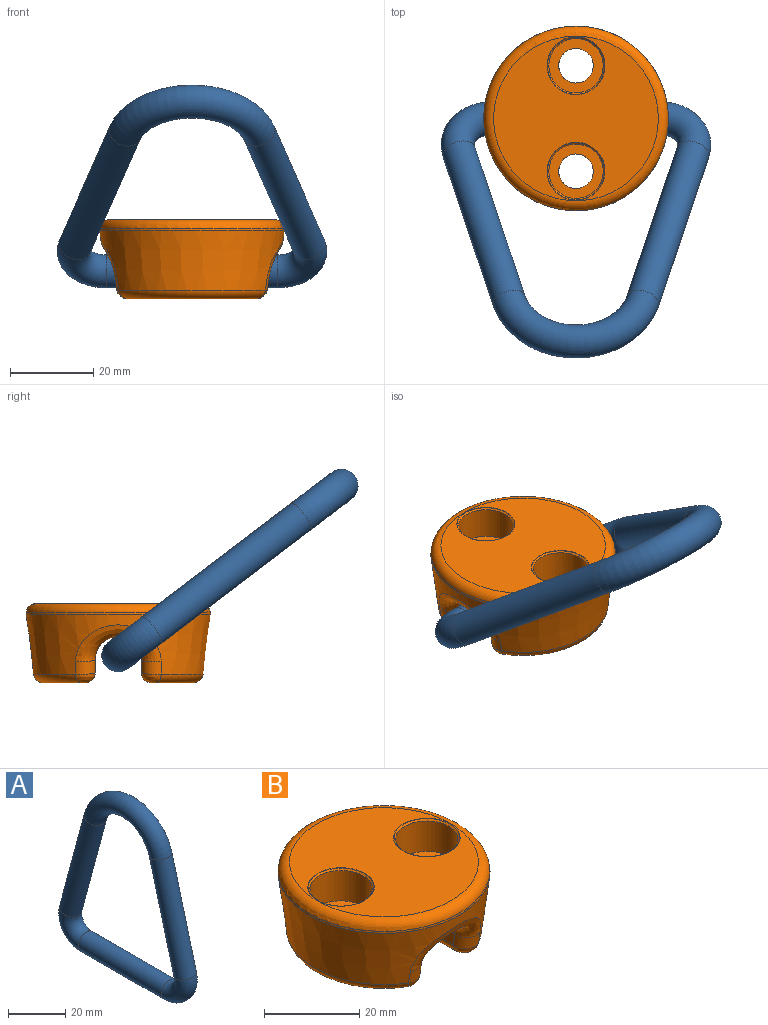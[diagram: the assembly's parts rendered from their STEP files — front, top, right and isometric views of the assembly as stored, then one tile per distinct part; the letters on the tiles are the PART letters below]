
ASSEMBLY  parts=2 mates=1
PART A: 6 faces, bbox 7.9x66.8x78.1 mm
  f0: cylinder r=3.97mm len=47.18mm, axis (0,0.26,0.97), area 1164.9mm2, adj f1,f5
  f1: torus R=7.94mm, axis (-1,0,0), area 362.7mm2, adj f0,f2
  f2: cylinder r=3.97mm len=41.05mm, axis (0,-1,0), area 1023.6mm2, adj f1,f3
  f3: torus R=7.94mm, axis (-1,0,0), area 362.7mm2, adj f2,f4
  f4: cylinder r=3.97mm len=47.18mm, axis (0,0.26,-0.97), area 1164.9mm2, adj f3,f5
  f5: torus R=16.67mm, axis (1,0,0), area 1088.2mm2, adj f0,f4
PART B: 44 faces, bbox 48x48x32 mm
  f0: plane 39.61x39.61mm, normal (0,0,1), area 926.8mm2, adj f22,f42,f43
  f1: cylinder r=5.56mm len=30.74mm, axis (0,1,0), area 274.6mm2, adj f6,f7,f9,f12,f32,f33,f34,f35
  f2: plane 31.44x10.14mm, normal (0,0,-1), area 170mm2, adj f14,f15,f16,f17,f39
  f3: cone r=22.23mm half-angle=7deg, axis (0,0,-1), area 63.1mm2, adj f4,f22
  f4: cone r=22.23mm half-angle=7deg, axis (0,0,1), area 1520.3mm2, adj f3,f8,f9,f10,f11,f12,f13,f16
  f5: plane 31.44x10.14mm, normal (0,0,-1), area 170mm2, adj f18,f19,f20,f21,f38
  f6: plane 30.74x3.18mm, normal (1,0,0), area 96.2mm2, adj f1,f8,f13,f15
  f7: plane 30.74x3.18mm, normal (-1,0,0), area 96.2mm2, adj f1,f10,f11,f20
  f8: bspline ~26.1x8.53mm, area 21mm2, adj f4,f6,f9,f17
  f9: bspline ~20.6x10.49mm, area 128mm2, adj f1,f4,f8,f10
  f10: bspline ~32.03x9.37mm, area 20.9mm2, adj f4,f7,f9,f21
  f11: bspline ~26.1x8.53mm, area 21mm2, adj f4,f7,f12,f18
  f12: bspline ~20.6x10.49mm, area 128mm2, adj f1,f4,f11,f13
  f13: bspline ~32.03x9.37mm, area 20.9mm2, adj f4,f6,f12,f14
  f14: bspline ~5.36x3.34mm, area 16.6mm2, adj f2,f13,f15,f16
  f15: cylinder r=2.39mm len=29.84mm, axis (0,-1,0), area 111.9mm2, adj f2,f6,f14,f17
  f16: torus R=18.09mm, axis (0,0,-1), area 140.7mm2, adj f2,f4,f14,f17
  f17: bspline ~5.37x3.89mm, area 16.6mm2, adj f2,f8,f15,f16
  f18: bspline ~5.37x3.89mm, area 16.6mm2, adj f5,f11,f19,f20
  f19: torus R=18.09mm, axis (0,0,-1), area 140.7mm2, adj f4,f5,f18,f21
  f20: cylinder r=2.39mm len=29.84mm, axis (0,1,0), area 111.9mm2, adj f5,f7,f18,f21
  f21: bspline ~5.36x3.34mm, area 16.6mm2, adj f5,f10,f19,f20
  f22: torus R=19.81mm, axis (0,0,1), area 460.6mm2, adj f0,f3
  f23: cylinder r=6.54mm len=13.08mm, axis (0,0,1), area 320.5mm2, adj f24,f41
  f24: plane 13.08x13.08mm, normal (0,0,1), area 79.9mm2, adj f23,f25
  f25: cylinder r=4.17mm len=10.49mm, axis (0,0,1), area 274.6mm2, adj f24,f38
  f26: cylinder r=6.54mm len=13.08mm, axis (0,0,1), area 320.5mm2, adj f27,f40
  f27: plane 13.08x13.08mm, normal (0,0,1), area 79.9mm2, adj f26,f28
  f28: cylinder r=4.17mm len=10.49mm, axis (0,0,1), area 274.6mm2, adj f27,f39
  f29: cylinder r=5.56mm len=14.86mm, axis (0,-1,0), area 273.5mm2, adj f30,f31,f32,f37
  f30: torus R=5.05mm, axis (0,-1,0), area 7.2mm2, adj f29,f34,f36
  f31: torus R=5.05mm, axis (0,-1,0), area 7.2mm2, adj f29,f33,f35
  f32: cylinder r=0.51mm len=14.86mm, axis (0,1,0), area 1.3mm2, adj f1,f29,f33,f34
  f33: bspline ~5.89x5.61mm, area 5mm2, adj f1,f31,f32,f35
  f34: bspline ~6.89x5.61mm, area 5mm2, adj f1,f30,f32,f36
  f35: bspline ~6.89x5.61mm, area 5mm2, adj f1,f31,f33,f37
  f36: bspline ~6.89x5.61mm, area 5mm2, adj f1,f30,f34,f37
  f37: cylinder r=0.51mm len=14.86mm, axis (0,-1,0), area 1.3mm2, adj f1,f29,f35,f36
  f38: cone r=4.55mm half-angle=45deg, axis (0,0,-1), area 14.7mm2, adj f5,f25
  f39: cone r=4.55mm half-angle=45deg, axis (0,0,-1), area 14.7mm2, adj f2,f28
  f40: cone r=6.54mm half-angle=45deg, axis (0,0,1), area 20.5mm2, adj f26,f43
  f41: cone r=6.54mm half-angle=45deg, axis (0,0,1), area 20.5mm2, adj f23,f42
  f42: torus R=6.97mm, axis (0,0,1), area 4.3mm2, adj f0,f41
  f43: torus R=6.97mm, axis (0,0,1), area 4.3mm2, adj f0,f40
PLACE A rot(axis=(0.41,0.41,-0.82),101.4deg) t=(0,-53.71,47.41)mm
PLACE B rot(axis=(0,0,1),90deg) t=(0,0,16.51)mm fixed
MATE revolute A.f2 <-> B.f29  axis (-1,0,0) through (0,0,6.58)mm
